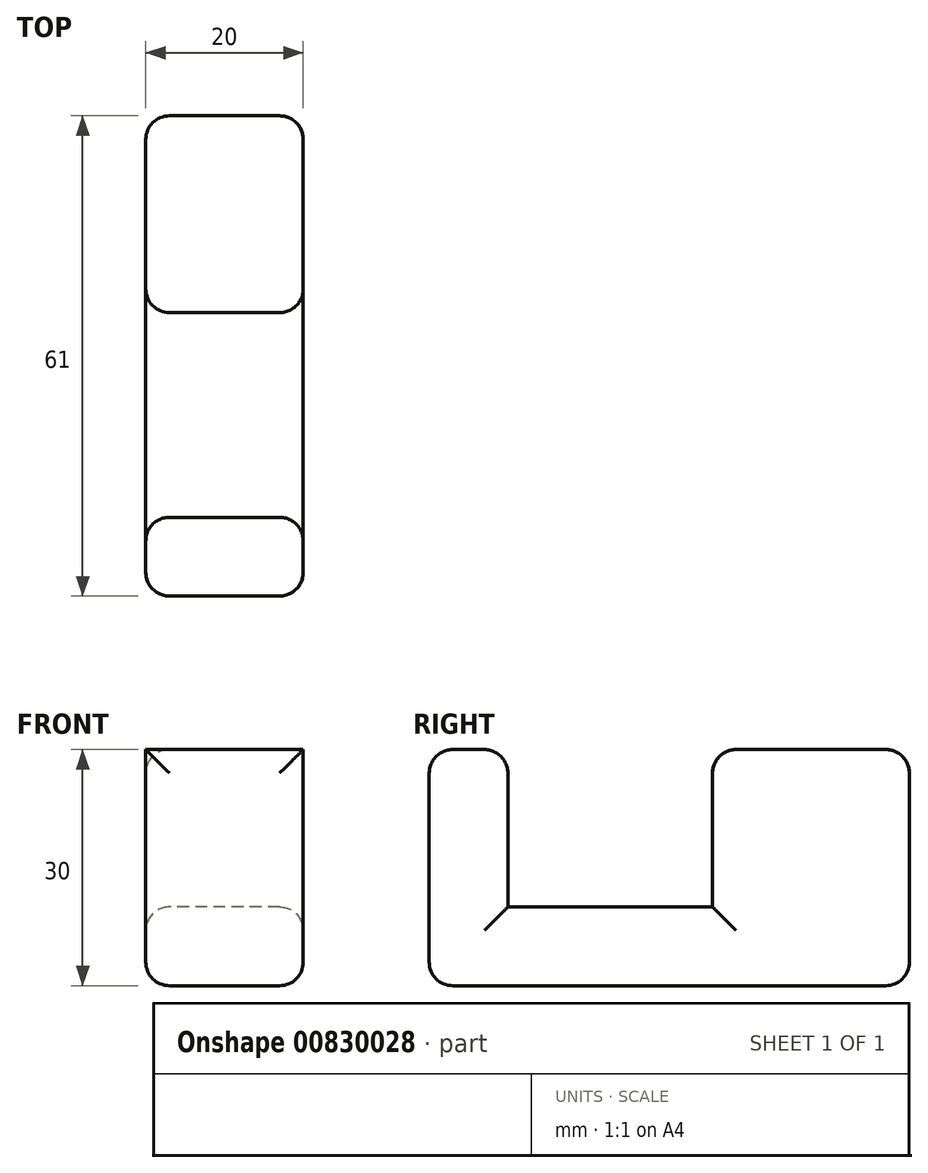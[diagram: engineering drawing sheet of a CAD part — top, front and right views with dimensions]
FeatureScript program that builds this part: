
annotation { "Feature Type Name" : "Feature", "Feature Type Description" : "" }
export const myFeature = defineFeature(function(context is Context, id is Id, definition is map)
    precondition{}
    {
        {
            var Q0;
            Q0=qCreatedBy(makeId("Right.planeOp"),FACE);
            var sketch = newSketch(context, id + "F0", { "sketchPlane" : qUnion([Q0])});
            skLineSegment(sketch, "E0", {"start": v(0, 0) * mm, "end": v(0, 30) * mm});
            skLineSegment(sketch, "E1", {"start": v(0, 30) * mm, "end": v(10, 30) * mm});
            skLineSegment(sketch, "E2", {"start": v(10, 30) * mm, "end": v(10, 10) * mm});
            skLineSegment(sketch, "E3", {"start": v(10, 10) * mm, "end": v(36, 10) * mm});
            skLineSegment(sketch, "E4", {"start": v(36, 10) * mm, "end": v(36, 30) * mm});
            skLineSegment(sketch, "E5", {"start": v(36, 30) * mm, "end": v(61, 30) * mm});
            skLineSegment(sketch, "E6", {"start": v(61, 30) * mm, "end": v(61, 0) * mm});
            skLineSegment(sketch, "E7", {"start": v(61, 0) * mm, "end": v(0, 0) * mm});
            skSolve(sketch);
        }
        {
            var Q0;
            Q0=makeQuery(id+"F0.imprint","IMPRINT",FACE,{"disambiguationData":[TD([[makeQuery(id+"F0.imprint","IMPRINT",EDGE,{"derivedFrom":sQuery(id+"F0.wireOp",EDGE,"E0")}),-1.0]])]});
            extrude(context, id + "F1", {"entities" : qUnion([Q0]), "depth" : 20 * mm, "offsetDistance" : 25 * mm});
        }
        {
            var Q0;
            Q0=makeQuery(id+"F1.opExtrude","CAP_EDGE",EDGE,{"disambiguationData":[OSD([sQuery(id+"F0.wireOp",EDGE,"E7")])],"isStart":false});
            var Q1;
            Q1=makeQuery(id+"F1.opExtrude","SWEPT_EDGE",EDGE,{"disambiguationData":[OSD([sQuery(id+"F0.wireOp",EDGE,"E0"),sQuery(id+"F0.wireOp",EDGE,"E7")])]});
            var Q2;
            Q2=makeQuery(id+"F1.opExtrude","CAP_EDGE",EDGE,{"disambiguationData":[OSD([sQuery(id+"F0.wireOp",EDGE,"E0")])],"isStart":false});
            var Q3;
            Q3=makeQuery(id+"F1.opExtrude","CAP_EDGE",EDGE,{"disambiguationData":[OSD([sQuery(id+"F0.wireOp",EDGE,"E0")])],"isStart":true});
            var Q4;
            Q4=makeQuery(id+"F1.opExtrude","CAP_EDGE",EDGE,{"disambiguationData":[OSD([sQuery(id+"F0.wireOp",EDGE,"E7")])],"isStart":true});
            var Q5;
            Q5=makeQuery(id+"F1.opExtrude","SWEPT_EDGE",EDGE,{"disambiguationData":[OSD([sQuery(id+"F0.wireOp",EDGE,"E0"),sQuery(id+"F0.wireOp",EDGE,"E1")])]});
            var Q6;
            Q6=makeQuery(id+"F1.opExtrude","SWEPT_EDGE",EDGE,{"disambiguationData":[OSD([sQuery(id+"F0.wireOp",EDGE,"E6"),sQuery(id+"F0.wireOp",EDGE,"E7")])]});
            var Q7;
            Q7=makeQuery(id+"F1.opExtrude","CAP_EDGE",EDGE,{"disambiguationData":[OSD([sQuery(id+"F0.wireOp",EDGE,"E6")])],"isStart":true});
            var Q8;
            Q8=makeQuery(id+"F1.opExtrude","CAP_EDGE",EDGE,{"disambiguationData":[OSD([sQuery(id+"F0.wireOp",EDGE,"E6")])],"isStart":false});
            var Q9;
            Q9=makeQuery(id+"F1.opExtrude","SWEPT_EDGE",EDGE,{"disambiguationData":[OSD([sQuery(id+"F0.wireOp",EDGE,"E5"),sQuery(id+"F0.wireOp",EDGE,"E6")])]});
            var Q10;
            Q10=makeQuery(id+"F1.opExtrude","CAP_EDGE",EDGE,{"disambiguationData":[OSD([sQuery(id+"F0.wireOp",EDGE,"E3")])],"isStart":false});
            var Q11;
            Q11=makeQuery(id+"F1.opExtrude","CAP_EDGE",EDGE,{"disambiguationData":[OSD([sQuery(id+"F0.wireOp",EDGE,"E4")])],"isStart":false});
            var Q12;
            Q12=makeQuery(id+"F1.opExtrude","CAP_EDGE",EDGE,{"disambiguationData":[OSD([sQuery(id+"F0.wireOp",EDGE,"E2")])],"isStart":false});
            var Q13;
            Q13=makeQuery(id+"F1.opExtrude","SWEPT_EDGE",EDGE,{"disambiguationData":[OSD([sQuery(id+"F0.wireOp",EDGE,"E1"),sQuery(id+"F0.wireOp",EDGE,"E2")])]});
            var Q14;
            Q14=makeQuery(id+"F1.opExtrude","SWEPT_EDGE",EDGE,{"disambiguationData":[OSD([sQuery(id+"F0.wireOp",EDGE,"E4"),sQuery(id+"F0.wireOp",EDGE,"E5")])]});
            var Q15;
            Q15=makeQuery(id+"F1.opExtrude","CAP_EDGE",EDGE,{"disambiguationData":[OSD([sQuery(id+"F0.wireOp",EDGE,"E5")])],"isStart":true});
            var Q16;
            Q16=makeQuery(id+"F1.opExtrude","CAP_EDGE",EDGE,{"disambiguationData":[OSD([sQuery(id+"F0.wireOp",EDGE,"E3")])],"isStart":true});
            var Q17;
            Q17=makeQuery(id+"F1.opExtrude","CAP_EDGE",EDGE,{"disambiguationData":[OSD([sQuery(id+"F0.wireOp",EDGE,"E4")])],"isStart":true});
            var Q18;
            Q18=makeQuery(id+"F1.opExtrude","CAP_EDGE",EDGE,{"disambiguationData":[OSD([sQuery(id+"F0.wireOp",EDGE,"E2")])],"isStart":true});
            fillet(context, id + "F2", {"entities" : qUnion([Q0, Q1, Q2, Q3, Q4, Q5, Q6, Q7, Q8, Q9, Q10, Q11, Q12, Q13, Q14, Q15, Q16, Q17, Q18]), "radius" : 3 * mm, "tangentPropagation" : true, "allowEdgeOverflow" : false});
        }
    });
